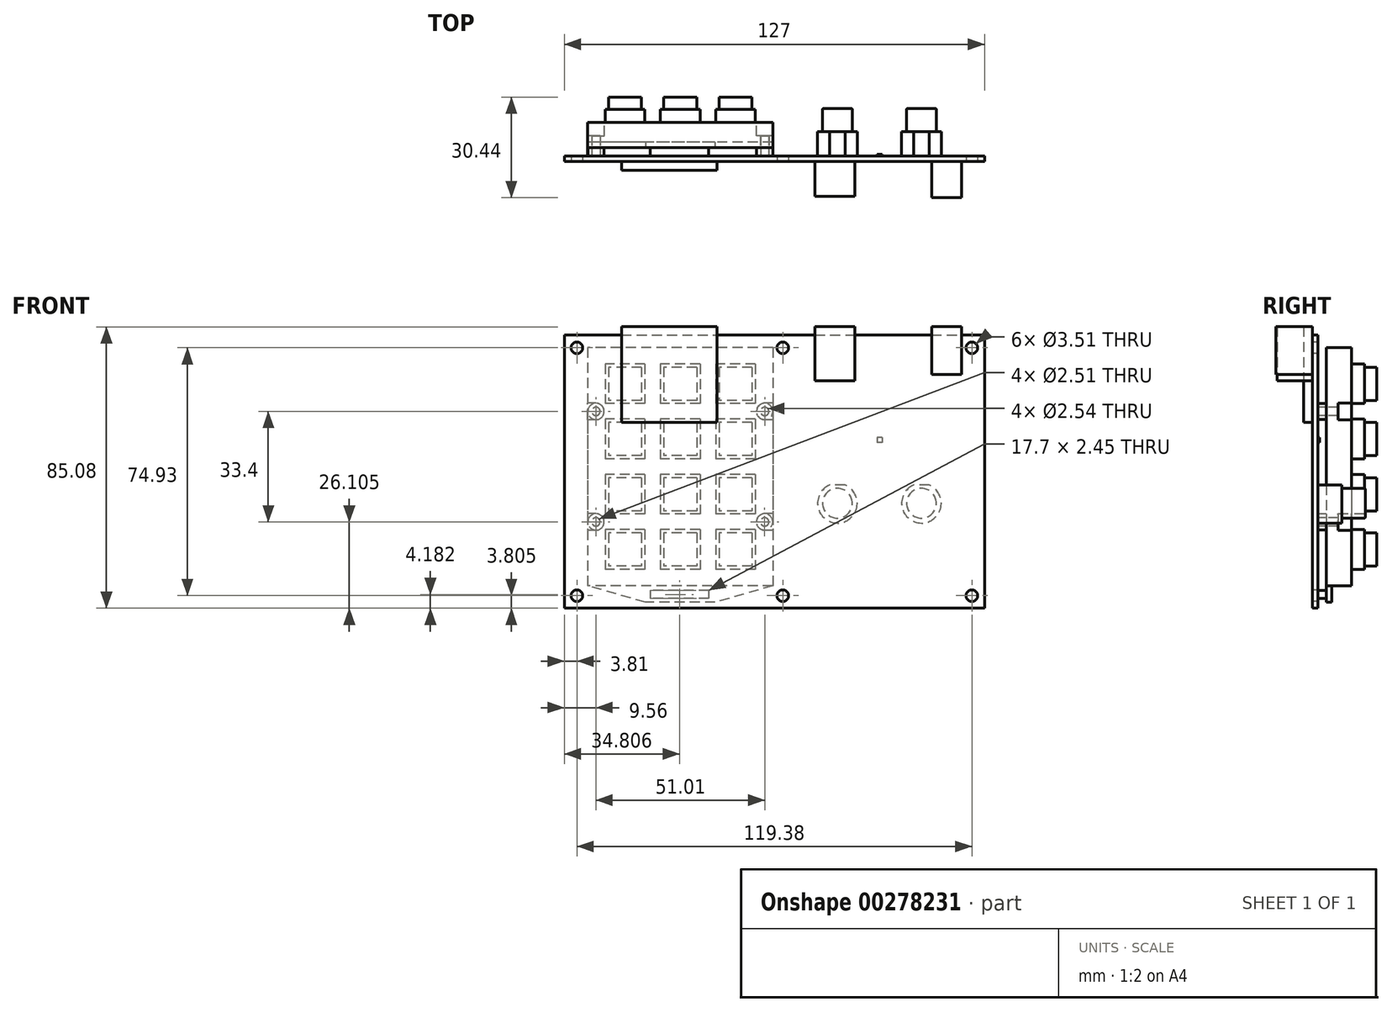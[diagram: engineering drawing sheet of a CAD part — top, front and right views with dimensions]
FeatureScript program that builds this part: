
annotation { "Feature Type Name" : "Feature", "Feature Type Description" : "" }
export const myFeature = defineFeature(function(context is Context, id is Id, definition is map)
    precondition{}
    {
        {
            var Q0;
            Q0=qCreatedBy(makeId("Front.planeOp"),FACE);
            var sketch = newSketch(context, id + "F0", { "sketchPlane" : qUnion([Q0])});
            skLineSegment(sketch, "E0.bottom", {"start": v(-63.5, 41.28) * mm, "end": v(63.5, 41.28) * mm});
            skLineSegment(sketch, "E0.top", {"start": v(-63.5, -41.28) * mm, "end": v(63.5, -41.28) * mm});
            skLineSegment(sketch, "E0.left", {"start": v(-63.5, 41.28) * mm, "end": v(-63.5, -41.28) * mm});
            skLineSegment(sketch, "E0.right", {"start": v(63.5, 41.28) * mm, "end": v(63.5, -41.28) * mm});
            skSolve(sketch);
        }
        {
            var Q0;
            Q0=makeQuery(id+"F0.imprint","IMPRINT",FACE,{"disambiguationData":[TD([[makeQuery(id+"F0.imprint","IMPRINT",EDGE,{"derivedFrom":sQuery(id+"F0.wireOp",EDGE,"E0.bottom")}),-1.0]])]});
            extrude(context, id + "F1", {"entities" : qUnion([Q0]), "depth" : 1.6 * mm});
        }
        {
            var Q0;
            Q0=makeQuery(id+"F1.opExtrude","CAP_FACE",FACE,{"disambiguationData":[OSD([sQuery(id+"F0.wireOp",EDGE,"E0.bottom"),sQuery(id+"F0.wireOp",EDGE,"E0.top"),sQuery(id+"F0.wireOp",EDGE,"E0.left"),sQuery(id+"F0.wireOp",EDGE,"E0.right")])],"isStart":false});
            var sketch = newSketch(context, id + "F2", { "sketchPlane" : qUnion([Q0])});
            skCircle(sketch, "E1", {"center": v(-59.7, 37.46) * mm, "radius": 1.75 * mm});
            skCircle(sketch, "E2", {"center": v(2.54, 37.46) * mm, "radius": 1.75 * mm});
            skCircle(sketch, "E3", {"center": v(59.7, 37.46) * mm, "radius": 1.75 * mm});
            skCircle(sketch, "E4", {"center": v(59.7, -37.47) * mm, "radius": 1.75 * mm});
            skCircle(sketch, "E5", {"center": v(2.54, -37.47) * mm, "radius": 1.75 * mm});
            skCircle(sketch, "E6", {"center": v(-59.7, -37.47) * mm, "radius": 1.75 * mm});
            skSolve(sketch);
        }
        {
            var Q0;
            Q0 = qSketchRegion(id + "F2", true);
            extrude(context, id + "F3", {"entities" : qUnion([Q0]), "operationType" : NewBodyOperationType.REMOVE, "oppositeDirection" : true, "depth" : 34.54 * mm});
        }
        {
            var Q0;
            Q0=makeQuery(id+"F1.opExtrude","CAP_FACE",FACE,{"disambiguationData":[OSD([sQuery(id+"F0.wireOp",EDGE,"E0.bottom"),sQuery(id+"F0.wireOp",EDGE,"E0.top"),sQuery(id+"F0.wireOp",EDGE,"E0.left"),sQuery(id+"F0.wireOp",EDGE,"E0.right")])],"isStart":false});
            var sketch = newSketch(context, id + "F4", { "sketchPlane" : qUnion([Q0])});
            skText(sketch, "E7", { "text": "Top\n", "fontName": "OpenSans-Regular.ttf"});
            const initialGuessF4  = {"E7": [-0.02127, 0.00143, 1, 0, 0.00758]};
            skSetInitialGuess(sketch, initialGuessF4);
            skSolve(sketch);
        }
        {
            var Q0;
            Q0=makeQuery(id+"F4.imprint","IMPRINT",FACE,{"disambiguationData":[TD([[makeQuery(id+"F4.imprint","IMPRINT",EDGE,{"derivedFrom":sQuery(id+"F4.wireOp",EDGE,"E7.sketch_text.stroke-0")}),1.0]])]});
            var sketch = newSketch(context, id + "F5", { "sketchPlane" : qUnion([Q0])});
            skLineSegment(sketch, "E8.bottom", {"start": v(-46.2, 43.82) * mm, "end": v(-17.3, 43.82) * mm});
            skLineSegment(sketch, "E8.top", {"start": v(-46.2, 14.92) * mm, "end": v(-17.3, 14.92) * mm});
            skLineSegment(sketch, "E8.left", {"start": v(-46.2, 43.82) * mm, "end": v(-46.2, 14.92) * mm});
            skLineSegment(sketch, "E8.right", {"start": v(-17.3, 43.82) * mm, "end": v(-17.3, 14.92) * mm});
            skLineSegment(sketch, "E9.bottom", {"start": v(12.27, 43.82) * mm, "end": v(24.3, 43.82) * mm});
            skLineSegment(sketch, "E9.top", {"start": v(12.27, 27.5) * mm, "end": v(24.3, 27.5) * mm});
            skLineSegment(sketch, "E9.left", {"start": v(12.27, 43.82) * mm, "end": v(12.27, 27.5) * mm});
            skLineSegment(sketch, "E9.right", {"start": v(24.3, 43.82) * mm, "end": v(24.3, 27.5) * mm});
            skLineSegment(sketch, "E10.bottom", {"start": v(47.52, 43.82) * mm, "end": v(56.51, 43.82) * mm});
            skLineSegment(sketch, "E10.top", {"start": v(47.52, 29.41) * mm, "end": v(56.51, 29.41) * mm});
            skLineSegment(sketch, "E10.left", {"start": v(47.52, 43.82) * mm, "end": v(47.52, 29.41) * mm});
            skLineSegment(sketch, "E10.right", {"start": v(56.51, 43.82) * mm, "end": v(56.51, 29.41) * mm});
            skSolve(sketch);
        }
        {
            var Q0;
            {var subQ0=sQuery(id+"F5.wireOp",EDGE,"E10.top");Q0=makeQuery(id+"F5.imprint","IMPRINT",FACE,{"disambiguationData":[TD([[makeQuery(id+"F5.imprint","IMPRINT",EDGE,{"derivedFrom":subQ0}),1.0]])]});}
            var Q1;
            {var subQ0=sQuery(id+"F5.wireOp",EDGE,"E10.bottom");Q1=makeQuery(id+"F5.imprint","IMPRINT",FACE,{"disambiguationData":[TD([[makeQuery(id+"F5.imprint","IMPRINT",EDGE,{"derivedFrom":subQ0}),-1.0]])]});}
            extrude(context, id + "F6", {"entities" : qUnion([Q0, Q1]), "operationType" : NewBodyOperationType.ADD, "depth" : 11 * mm});
        }
        {
            var Q0;
            {var subQ0=sQuery(id+"F5.wireOp",EDGE,"E9.top");Q0=makeQuery(id+"F5.imprint","IMPRINT",FACE,{"disambiguationData":[TD([[makeQuery(id+"F5.imprint","IMPRINT",EDGE,{"derivedFrom":subQ0}),1.0]])]});}
            var Q1;
            {var subQ0=sQuery(id+"F5.wireOp",EDGE,"E9.bottom");Q1=makeQuery(id+"F5.imprint","IMPRINT",FACE,{"disambiguationData":[TD([[makeQuery(id+"F5.imprint","IMPRINT",EDGE,{"derivedFrom":subQ0}),-1.0]])]});}
            extrude(context, id + "F7", {"entities" : qUnion([Q0, Q1]), "operationType" : NewBodyOperationType.ADD, "depth" : 10.62 * mm});
        }
        {
            var Q0;
            {var subQ0=sQuery(id+"F5.wireOp",EDGE,"E8.top");Q0=makeQuery(id+"F5.imprint","IMPRINT",FACE,{"disambiguationData":[TD([[makeQuery(id+"F5.imprint","IMPRINT",EDGE,{"derivedFrom":subQ0}),1.0]])]});}
            var Q1;
            {var subQ0=sQuery(id+"F5.wireOp",EDGE,"E8.bottom");Q1=makeQuery(id+"F5.imprint","IMPRINT",FACE,{"disambiguationData":[TD([[makeQuery(id+"F5.imprint","IMPRINT",EDGE,{"derivedFrom":subQ0}),-1.0]])]});}
            extrude(context, id + "F8", {"entities" : qUnion([Q0, Q1]), "operationType" : NewBodyOperationType.ADD, "depth" : 2.7 * mm});
        }
        {
            var Q0;
            Q0=makeQuery(id+"F1.opExtrude","CAP_FACE",FACE,{"disambiguationData":[OSD([sQuery(id+"F0.wireOp",EDGE,"E0.bottom"),sQuery(id+"F0.wireOp",EDGE,"E0.top"),sQuery(id+"F0.wireOp",EDGE,"E0.left"),sQuery(id+"F0.wireOp",EDGE,"E0.right")])],"isStart":true});
            var sketch = newSketch(context, id + "F9", { "sketchPlane" : qUnion([Q0])});
            skArc(sketch, "E11", {"start": v(-46.8, -4.01) * mm, "mid": v(-44.45, -15.52) * mm, "end": v(-42.1, -4.01) * mm});
            skArc(sketch, "E12", {"start": v(-21.4, -4.01) * mm, "mid": v(-19.05, -15.52) * mm, "end": v(-16.7, -4.01) * mm});
            skLineSegment(sketch, "E13", {"start": v(-46.8, -4.01) * mm, "end": v(-42.1, -4.01) * mm});
            skLineSegment(sketch, "E14.trimOffspring", {"start": v(-21.4, -4.01) * mm, "end": v(-16.7, -4.01) * mm});
            skSolve(sketch);
        }
        {
            var Q0;
            Q0 = qSketchRegion(id + "F9", true);
            extrude(context, id + "F10", {"entities" : qUnion([Q0]), "operationType" : NewBodyOperationType.ADD, "depth" : 7.34 * mm});
        }
        {
            var Q0;
            Q0=makeQuery(id+"F10.opExtrude","CAP_FACE",FACE,{"disambiguationData":[OSD([sQuery(id+"F9.wireOp",EDGE,"E11"),sQuery(id+"F9.wireOp",EDGE,"E13")])],"isStart":false});
            var sketch = newSketch(context, id + "F11", { "sketchPlane" : qUnion([Q0])});
            skCircle(sketch, "E15", {"center": v(-44.45, -9.53) * mm, "radius": 4.5 * mm});
            skCircle(sketch, "E16", {"center": v(-19.05, -9.53) * mm, "radius": 4.5 * mm});
            skSolve(sketch);
        }
        {
            var Q0;
            Q0 = qSketchRegion(id + "F11", true);
            extrude(context, id + "F12", {"entities" : qUnion([Q0]), "operationType" : NewBodyOperationType.ADD, "depth" : 7 * mm});
        }
        {
            var Q0;
            Q0=makeQuery(id+"F12.opExtrude","CAP_EDGE",EDGE,{"disambiguationData":[OSD([sQuery(id+"F11.wireOp",EDGE,"E15")])],"isStart":false});
            var Q1;
            Q1=makeQuery(id+"F12.opExtrude","CAP_EDGE",EDGE,{"disambiguationData":[OSD([sQuery(id+"F11.wireOp",EDGE,"E16")])],"isStart":false});
            fillet(context, id + "F13", {"entities" : qUnion([Q0, Q1]), "radius" : 0.25 * mm, "tangentPropagation" : true, "allowEdgeOverflow" : false});
        }
        {
            var Q0;
            Q0=makeQuery(id+"F1.opExtrude","CAP_FACE",FACE,{"disambiguationData":[OSD([sQuery(id+"F0.wireOp",EDGE,"E0.bottom"),sQuery(id+"F0.wireOp",EDGE,"E0.top"),sQuery(id+"F0.wireOp",EDGE,"E0.left"),sQuery(id+"F0.wireOp",EDGE,"E0.right")])],"isStart":true});
            var sketch = newSketch(context, id + "F14", { "sketchPlane" : qUnion([Q0])});
            skLineSegment(sketch, "E17.bottom", {"start": v(-32.51, 10.31) * mm, "end": v(-30.99, 10.31) * mm});
            skLineSegment(sketch, "E17.top", {"start": v(-32.51, 8.76) * mm, "end": v(-30.99, 8.76) * mm});
            skLineSegment(sketch, "E17.left", {"start": v(-32.51, 10.31) * mm, "end": v(-32.51, 8.76) * mm});
            skLineSegment(sketch, "E17.right", {"start": v(-30.99, 10.31) * mm, "end": v(-30.99, 8.76) * mm});
            skSolve(sketch);
        }
        {
            var Q0;
            Q0 = qSketchRegion(id + "F14", true);
            extrude(context, id + "F15", {"entities" : qUnion([Q0]), "operationType" : NewBodyOperationType.ADD, "depth" : 0.53 * mm});
        }
        {
            var Q0;
            Q0=makeQuery(id+"F1.opExtrude","CAP_FACE",FACE,{"disambiguationData":[OSD([sQuery(id+"F0.wireOp",EDGE,"E0.bottom"),sQuery(id+"F0.wireOp",EDGE,"E0.top"),sQuery(id+"F0.wireOp",EDGE,"E0.left"),sQuery(id+"F0.wireOp",EDGE,"E0.right")])],"isStart":true});
            var sketch = newSketch(context, id + "F16", { "sketchPlane" : qUnion([Q0])});
            skLineSegment(sketch, "E18.bottom", {"start": v(0.45, 37.53) * mm, "end": v(56.43, 37.53) * mm});
            skLineSegment(sketch, "E18.top", {"start": v(0.45, -34.47) * mm, "end": v(56.43, -34.47) * mm});
            skLineSegment(sketch, "E18.left", {"start": v(0.45, 37.53) * mm, "end": v(0.45, -34.47) * mm});
            skLineSegment(sketch, "E18.right", {"start": v(56.43, 37.53) * mm, "end": v(56.43, -34.47) * mm});
            skCircle(sketch, "E19", {"center": v(2.93, 18.23) * mm, "radius": 1.27 * mm});
            skCircle(sketch, "E20", {"center": v(2.94, -15.16) * mm, "radius": 1.27 * mm});
            skCircle(sketch, "E21", {"center": v(53.93, 18.23) * mm, "radius": 1.27 * mm});
            skCircle(sketch, "E22", {"center": v(53.94, -15.16) * mm, "radius": 1.27 * mm});
            skLineSegment(sketch, "E23", {"start": v(0.45, -34.47) * mm, "end": v(17.95, -39.46) * mm});
            skLineSegment(sketch, "E24", {"start": v(17.95, -39.46) * mm, "end": v(38.95, -39.46) * mm});
            skLineSegment(sketch, "E25", {"start": v(38.95, -39.46) * mm, "end": v(56.43, -34.47) * mm});
            skPoint(sketch, "E26", {"position": v(28.45, -37.47) * mm});
            skSolve(sketch);
        }
        {
            var Q0;
            Q0=makeQuery(id+"F16.imprint","IMPRINT",FACE,{"disambiguationData":[TD([[makeQuery(id+"F16.imprint","IMPRINT",EDGE,{"derivedFrom":sQuery(id+"F16.wireOp",EDGE,"E18.bottom")}),-1.0]])]});
            extrude(context, id + "F17", {"entities" : qUnion([Q0]), "depth" : 10.14 * mm, "hasSecondDirection" : true, "secondDirectionOppositeDirection" : false, "secondDirectionDepth" : 2.54 * mm});
        }
        {
            var Q0;
            Q0=makeQuery(id+"F16.imprint","IMPRINT",FACE,{"disambiguationData":[TD([[makeQuery(id+"F16.imprint","IMPRINT",EDGE,{"derivedFrom":sQuery(id+"F16.wireOp",EDGE,"E18.top")}),-1.0]])]});
            extrude(context, id + "F18", {"entities" : qUnion([Q0]), "operationType" : NewBodyOperationType.ADD, "depth" : 4.2 * mm, "hasSecondDirection" : true, "secondDirectionOppositeDirection" : false, "secondDirectionDepth" : 2.54 * mm});
        }
        {
            var Q0;
            Q0=makeQuery(id+"F17.opExtrude","CAP_FACE",FACE,{"disambiguationData":[OSD([sQuery(id+"F16.wireOp",EDGE,"E18.bottom"),sQuery(id+"F16.wireOp",EDGE,"E18.top"),sQuery(id+"F16.wireOp",EDGE,"E18.left"),sQuery(id+"F16.wireOp",EDGE,"E18.right"),sQuery(id+"F16.wireOp",EDGE,"E19"),sQuery(id+"F16.wireOp",EDGE,"E20"),sQuery(id+"F16.wireOp",EDGE,"E21"),sQuery(id+"F16.wireOp",EDGE,"E22")])],"isStart":false});
            var sketch = newSketch(context, id + "F19", { "sketchPlane" : qUnion([Q0])});
            skArc(sketch, "E27", {"start": v(53.93, 20.74) * mm, "mid": v(51.43, 18.23) * mm, "end": v(53.93, 15.73) * mm});
            skArc(sketch, "E28", {"start": v(53.94, -12.66) * mm, "mid": v(51.44, -15.16) * mm, "end": v(53.94, -17.67) * mm});
            skArc(sketch, "E29", {"start": v(0.45, -14.95) * mm, "mid": v(0.44, -15.16) * mm, "end": v(0.45, -15.38) * mm});
            skArc(sketch, "E30", {"start": v(0.45, 18.55) * mm, "mid": v(0.43, 18.23) * mm, "end": v(0.45, 17.92) * mm});
            skLineSegment(sketch, "E31", {"start": v(0.45, 20.74) * mm, "end": v(2.93, 20.74) * mm});
            skLineSegment(sketch, "E32", {"start": v(0.45, 15.73) * mm, "end": v(2.93, 15.73) * mm});
            skLineSegment(sketch, "E33", {"start": v(0.45, -12.66) * mm, "end": v(2.94, -12.66) * mm});
            skLineSegment(sketch, "E34", {"start": v(0.45, -17.67) * mm, "end": v(2.94, -17.67) * mm});
            skLineSegment(sketch, "E35", {"start": v(0.45, 20.74) * mm, "end": v(0.45, 15.73) * mm});
            skLineSegment(sketch, "E36", {"start": v(56.43, 20.74) * mm, "end": v(56.43, 15.73) * mm});
            skLineSegment(sketch, "E37", {"start": v(0.45, -12.66) * mm, "end": v(0.45, -17.67) * mm});
            skLineSegment(sketch, "E38", {"start": v(56.43, -12.66) * mm, "end": v(56.43, -17.67) * mm});
            skArc(sketch, "E39.trimOffspring", {"start": v(2.93, 15.73) * mm, "mid": v(5.43, 18.23) * mm, "end": v(2.93, 20.74) * mm});
            skArc(sketch, "E40.trimOffspring", {"start": v(56.43, 18.12) * mm, "mid": v(56.43, 18.23) * mm, "end": v(56.43, 18.35) * mm});
            skArc(sketch, "E41.trimOffspring", {"start": v(56.43, -15.42) * mm, "mid": v(56.44, -15.16) * mm, "end": v(56.43, -14.91) * mm});
            skLineSegment(sketch, "E42.trimOffspring", {"start": v(53.93, 15.73) * mm, "end": v(56.43, 15.73) * mm});
            skLineSegment(sketch, "E43.trimOffspring", {"start": v(53.93, 20.74) * mm, "end": v(56.43, 20.74) * mm});
            skArc(sketch, "E44.trimOffspring", {"start": v(2.94, -17.67) * mm, "mid": v(5.44, -15.16) * mm, "end": v(2.94, -12.66) * mm});
            skLineSegment(sketch, "E45.trimOffspring", {"start": v(53.94, -17.67) * mm, "end": v(56.43, -17.67) * mm});
            skLineSegment(sketch, "E46.trimOffspring", {"start": v(53.94, -12.66) * mm, "end": v(56.43, -12.66) * mm});
            skSolve(sketch);
        }
        {
            var Q0;
            Q0 = qSketchRegion(id + "F19", true);
            extrude(context, id + "F20", {"entities" : qUnion([Q0]), "operationType" : NewBodyOperationType.REMOVE, "oppositeDirection" : true, "depth" : 4 * mm});
        }
        {
            var Q0;
            Q0=makeQuery(id+"F17.opExtrude","CAP_FACE",FACE,{"disambiguationData":[OSD([sQuery(id+"F16.wireOp",EDGE,"E18.bottom"),sQuery(id+"F16.wireOp",EDGE,"E18.top"),sQuery(id+"F16.wireOp",EDGE,"E18.left"),sQuery(id+"F16.wireOp",EDGE,"E18.right"),sQuery(id+"F16.wireOp",EDGE,"E19"),sQuery(id+"F16.wireOp",EDGE,"E20"),sQuery(id+"F16.wireOp",EDGE,"E21"),sQuery(id+"F16.wireOp",EDGE,"E22")])],"isStart":false});
            var sketch = newSketch(context, id + "F21", { "sketchPlane" : qUnion([Q0])});
            skLineSegment(sketch, "E47.bottom", {"start": v(5.75, -17.52) * mm, "end": v(17.75, -17.52) * mm});
            skLineSegment(sketch, "E47.top", {"start": v(5.75, -29.52) * mm, "end": v(17.75, -29.52) * mm});
            skLineSegment(sketch, "E47.left", {"start": v(5.75, -17.52) * mm, "end": v(5.75, -29.52) * mm});
            skLineSegment(sketch, "E47.right", {"start": v(17.75, -17.52) * mm, "end": v(17.75, -29.52) * mm});
            skLineSegment(sketch, "E48.0.1.0", {"start": v(5.75, -0.82) * mm, "end": v(17.75, -0.82) * mm});
            skLineSegment(sketch, "E48.0.1.1", {"start": v(17.75, -0.82) * mm, "end": v(17.75, -12.82) * mm});
            skLineSegment(sketch, "E48.0.1.2", {"start": v(5.75, -12.82) * mm, "end": v(17.75, -12.82) * mm});
            skLineSegment(sketch, "E48.0.1.3", {"start": v(5.75, -0.82) * mm, "end": v(5.75, -12.82) * mm});
            skLineSegment(sketch, "E48.0.2.0", {"start": v(5.75, 15.88) * mm, "end": v(17.75, 15.88) * mm});
            skLineSegment(sketch, "E48.0.2.1", {"start": v(17.75, 15.88) * mm, "end": v(17.75, 3.88) * mm});
            skLineSegment(sketch, "E48.0.2.2", {"start": v(5.75, 3.88) * mm, "end": v(17.75, 3.88) * mm});
            skLineSegment(sketch, "E48.0.2.3", {"start": v(5.75, 15.88) * mm, "end": v(5.75, 3.88) * mm});
            skLineSegment(sketch, "E48.0.3.0", {"start": v(5.75, 32.58) * mm, "end": v(17.75, 32.58) * mm});
            skLineSegment(sketch, "E48.0.3.1", {"start": v(17.75, 32.58) * mm, "end": v(17.75, 20.58) * mm});
            skLineSegment(sketch, "E48.0.3.2", {"start": v(5.75, 20.58) * mm, "end": v(17.75, 20.58) * mm});
            skLineSegment(sketch, "E48.0.3.3", {"start": v(5.75, 32.58) * mm, "end": v(5.75, 20.58) * mm});
            skLineSegment(sketch, "E48.1.0.0", {"start": v(22.45, -17.52) * mm, "end": v(34.45, -17.52) * mm});
            skLineSegment(sketch, "E48.1.0.1", {"start": v(34.45, -17.52) * mm, "end": v(34.45, -29.52) * mm});
            skLineSegment(sketch, "E48.1.0.2", {"start": v(22.45, -29.52) * mm, "end": v(34.45, -29.52) * mm});
            skLineSegment(sketch, "E48.1.0.3", {"start": v(22.45, -17.52) * mm, "end": v(22.45, -29.52) * mm});
            skLineSegment(sketch, "E48.1.1.0", {"start": v(22.45, -0.82) * mm, "end": v(34.45, -0.82) * mm});
            skLineSegment(sketch, "E48.1.1.1", {"start": v(34.45, -0.82) * mm, "end": v(34.45, -12.82) * mm});
            skLineSegment(sketch, "E48.1.1.2", {"start": v(22.45, -12.82) * mm, "end": v(34.45, -12.82) * mm});
            skLineSegment(sketch, "E48.1.1.3", {"start": v(22.45, -0.82) * mm, "end": v(22.45, -12.82) * mm});
            skLineSegment(sketch, "E48.1.2.0", {"start": v(22.45, 15.88) * mm, "end": v(34.45, 15.88) * mm});
            skLineSegment(sketch, "E48.1.2.1", {"start": v(34.45, 15.88) * mm, "end": v(34.45, 3.88) * mm});
            skLineSegment(sketch, "E48.1.2.2", {"start": v(22.45, 3.88) * mm, "end": v(34.45, 3.88) * mm});
            skLineSegment(sketch, "E48.1.2.3", {"start": v(22.45, 15.88) * mm, "end": v(22.45, 3.88) * mm});
            skLineSegment(sketch, "E48.1.3.0", {"start": v(22.45, 32.58) * mm, "end": v(34.45, 32.58) * mm});
            skLineSegment(sketch, "E48.1.3.1", {"start": v(34.45, 32.58) * mm, "end": v(34.45, 20.58) * mm});
            skLineSegment(sketch, "E48.1.3.2", {"start": v(22.45, 20.58) * mm, "end": v(34.45, 20.58) * mm});
            skLineSegment(sketch, "E48.1.3.3", {"start": v(22.45, 32.58) * mm, "end": v(22.45, 20.58) * mm});
            skLineSegment(sketch, "E48.2.0.0", {"start": v(39.15, -17.52) * mm, "end": v(51.15, -17.52) * mm});
            skLineSegment(sketch, "E48.2.0.1", {"start": v(51.15, -17.52) * mm, "end": v(51.15, -29.52) * mm});
            skLineSegment(sketch, "E48.2.0.2", {"start": v(39.15, -29.52) * mm, "end": v(51.15, -29.52) * mm});
            skLineSegment(sketch, "E48.2.0.3", {"start": v(39.15, -17.52) * mm, "end": v(39.15, -29.52) * mm});
            skLineSegment(sketch, "E48.2.1.0", {"start": v(39.15, -0.82) * mm, "end": v(51.15, -0.82) * mm});
            skLineSegment(sketch, "E48.2.1.1", {"start": v(51.15, -0.82) * mm, "end": v(51.15, -12.82) * mm});
            skLineSegment(sketch, "E48.2.1.2", {"start": v(39.15, -12.82) * mm, "end": v(51.15, -12.82) * mm});
            skLineSegment(sketch, "E48.2.1.3", {"start": v(39.15, -0.82) * mm, "end": v(39.15, -12.82) * mm});
            skLineSegment(sketch, "E48.2.2.0", {"start": v(39.15, 15.88) * mm, "end": v(51.15, 15.88) * mm});
            skLineSegment(sketch, "E48.2.2.1", {"start": v(51.15, 15.88) * mm, "end": v(51.15, 3.88) * mm});
            skLineSegment(sketch, "E48.2.2.2", {"start": v(39.15, 3.88) * mm, "end": v(51.15, 3.88) * mm});
            skLineSegment(sketch, "E48.2.2.3", {"start": v(39.15, 15.88) * mm, "end": v(39.15, 3.88) * mm});
            skLineSegment(sketch, "E48.2.3.0", {"start": v(39.15, 32.58) * mm, "end": v(51.15, 32.58) * mm});
            skLineSegment(sketch, "E48.2.3.1", {"start": v(51.15, 32.58) * mm, "end": v(51.15, 20.58) * mm});
            skLineSegment(sketch, "E48.2.3.2", {"start": v(39.15, 20.58) * mm, "end": v(51.15, 20.58) * mm});
            skLineSegment(sketch, "E48.2.3.3", {"start": v(39.15, 32.58) * mm, "end": v(39.15, 20.58) * mm});
            skLineSegment(sketch, "E48.direction1", {"start": v(5.75, -29.52) * mm, "end": v(22.45, -29.52) * mm, "construction": true});
            skLineSegment(sketch, "E48.direction2", {"start": v(5.75, -29.52) * mm, "end": v(5.75, -12.82) * mm, "construction": true});
            skLineSegment(sketch, "E49.bottom", {"start": v(6.75, -18.52) * mm, "end": v(16.75, -18.52) * mm});
            skLineSegment(sketch, "E49.top", {"start": v(6.75, -28.52) * mm, "end": v(16.75, -28.52) * mm});
            skLineSegment(sketch, "E49.left", {"start": v(6.75, -18.52) * mm, "end": v(6.75, -28.52) * mm});
            skLineSegment(sketch, "E49.right", {"start": v(16.75, -18.52) * mm, "end": v(16.75, -28.52) * mm});
            skLineSegment(sketch, "E50.0.1.0", {"start": v(6.75, -1.82) * mm, "end": v(16.75, -1.82) * mm});
            skLineSegment(sketch, "E50.0.1.1", {"start": v(6.75, -1.82) * mm, "end": v(6.75, -11.82) * mm});
            skLineSegment(sketch, "E50.0.1.2", {"start": v(6.75, -11.82) * mm, "end": v(16.75, -11.82) * mm});
            skLineSegment(sketch, "E50.0.1.3", {"start": v(16.75, -1.82) * mm, "end": v(16.75, -11.82) * mm});
            skLineSegment(sketch, "E50.0.2.0", {"start": v(6.75, 14.88) * mm, "end": v(16.75, 14.88) * mm});
            skLineSegment(sketch, "E50.0.2.1", {"start": v(6.75, 14.88) * mm, "end": v(6.75, 4.88) * mm});
            skLineSegment(sketch, "E50.0.2.2", {"start": v(6.75, 4.88) * mm, "end": v(16.75, 4.88) * mm});
            skLineSegment(sketch, "E50.0.2.3", {"start": v(16.75, 14.88) * mm, "end": v(16.75, 4.88) * mm});
            skLineSegment(sketch, "E50.0.3.0", {"start": v(6.75, 31.58) * mm, "end": v(16.75, 31.58) * mm});
            skLineSegment(sketch, "E50.0.3.1", {"start": v(6.75, 31.58) * mm, "end": v(6.75, 21.58) * mm});
            skLineSegment(sketch, "E50.0.3.2", {"start": v(6.75, 21.58) * mm, "end": v(16.75, 21.58) * mm});
            skLineSegment(sketch, "E50.0.3.3", {"start": v(16.75, 31.58) * mm, "end": v(16.75, 21.58) * mm});
            skLineSegment(sketch, "E50.1.0.0", {"start": v(23.45, -18.52) * mm, "end": v(33.45, -18.52) * mm});
            skLineSegment(sketch, "E50.1.0.1", {"start": v(23.45, -18.52) * mm, "end": v(23.45, -28.52) * mm});
            skLineSegment(sketch, "E50.1.0.2", {"start": v(23.45, -28.52) * mm, "end": v(33.45, -28.52) * mm});
            skLineSegment(sketch, "E50.1.0.3", {"start": v(33.45, -18.52) * mm, "end": v(33.45, -28.52) * mm});
            skLineSegment(sketch, "E50.1.1.0", {"start": v(23.45, -1.82) * mm, "end": v(33.45, -1.82) * mm});
            skLineSegment(sketch, "E50.1.1.1", {"start": v(23.45, -1.82) * mm, "end": v(23.45, -11.82) * mm});
            skLineSegment(sketch, "E50.1.1.2", {"start": v(23.45, -11.82) * mm, "end": v(33.45, -11.82) * mm});
            skLineSegment(sketch, "E50.1.1.3", {"start": v(33.45, -1.82) * mm, "end": v(33.45, -11.82) * mm});
            skLineSegment(sketch, "E50.1.2.0", {"start": v(23.45, 14.88) * mm, "end": v(33.45, 14.88) * mm});
            skLineSegment(sketch, "E50.1.2.1", {"start": v(23.45, 14.88) * mm, "end": v(23.45, 4.88) * mm});
            skLineSegment(sketch, "E50.1.2.2", {"start": v(23.45, 4.88) * mm, "end": v(33.45, 4.88) * mm});
            skLineSegment(sketch, "E50.1.2.3", {"start": v(33.45, 14.88) * mm, "end": v(33.45, 4.88) * mm});
            skLineSegment(sketch, "E50.1.3.0", {"start": v(23.45, 31.58) * mm, "end": v(33.45, 31.58) * mm});
            skLineSegment(sketch, "E50.1.3.1", {"start": v(23.45, 31.58) * mm, "end": v(23.45, 21.58) * mm});
            skLineSegment(sketch, "E50.1.3.2", {"start": v(23.45, 21.58) * mm, "end": v(33.45, 21.58) * mm});
            skLineSegment(sketch, "E50.1.3.3", {"start": v(33.45, 31.58) * mm, "end": v(33.45, 21.58) * mm});
            skLineSegment(sketch, "E50.2.0.0", {"start": v(40.15, -18.52) * mm, "end": v(50.15, -18.52) * mm});
            skLineSegment(sketch, "E50.2.0.1", {"start": v(40.15, -18.52) * mm, "end": v(40.15, -28.52) * mm});
            skLineSegment(sketch, "E50.2.0.2", {"start": v(40.15, -28.52) * mm, "end": v(50.15, -28.52) * mm});
            skLineSegment(sketch, "E50.2.0.3", {"start": v(50.15, -18.52) * mm, "end": v(50.15, -28.52) * mm});
            skLineSegment(sketch, "E50.2.1.0", {"start": v(40.15, -1.82) * mm, "end": v(50.15, -1.82) * mm});
            skLineSegment(sketch, "E50.2.1.1", {"start": v(40.15, -1.82) * mm, "end": v(40.15, -11.82) * mm});
            skLineSegment(sketch, "E50.2.1.2", {"start": v(40.15, -11.82) * mm, "end": v(50.15, -11.82) * mm});
            skLineSegment(sketch, "E50.2.1.3", {"start": v(50.15, -1.82) * mm, "end": v(50.15, -11.82) * mm});
            skLineSegment(sketch, "E50.2.2.0", {"start": v(40.15, 14.88) * mm, "end": v(50.15, 14.88) * mm});
            skLineSegment(sketch, "E50.2.2.1", {"start": v(40.15, 14.88) * mm, "end": v(40.15, 4.88) * mm});
            skLineSegment(sketch, "E50.2.2.2", {"start": v(40.15, 4.88) * mm, "end": v(50.15, 4.88) * mm});
            skLineSegment(sketch, "E50.2.2.3", {"start": v(50.15, 14.88) * mm, "end": v(50.15, 4.88) * mm});
            skLineSegment(sketch, "E50.2.3.0", {"start": v(40.15, 31.58) * mm, "end": v(50.15, 31.58) * mm});
            skLineSegment(sketch, "E50.2.3.1", {"start": v(40.15, 31.58) * mm, "end": v(40.15, 21.58) * mm});
            skLineSegment(sketch, "E50.2.3.2", {"start": v(40.15, 21.58) * mm, "end": v(50.15, 21.58) * mm});
            skLineSegment(sketch, "E50.2.3.3", {"start": v(50.15, 31.58) * mm, "end": v(50.15, 21.58) * mm});
            skLineSegment(sketch, "E50.direction1", {"start": v(6.75, -28.52) * mm, "end": v(23.45, -28.52) * mm, "construction": true});
            skLineSegment(sketch, "E50.direction2", {"start": v(6.75, -28.52) * mm, "end": v(6.75, -11.82) * mm, "construction": true});
            skSolve(sketch);
        }
        {
            var Q0;
            Q0 = qSketchRegion(id + "F21", true);
            extrude(context, id + "F22", {"entities" : qUnion([Q0]), "operationType" : NewBodyOperationType.ADD, "depth" : 4 * mm});
        }
        {
            var Q0;
            Q0=makeQuery(id+"F21.imprint","IMPRINT",FACE,{"disambiguationData":[TD([[makeQuery(id+"F21.imprint","IMPRINT",EDGE,{"derivedFrom":sQuery(id+"F21.wireOp",EDGE,"E49.bottom")}),-1.0]])]});
            var Q1;
            Q1=makeQuery(id+"F21.imprint","IMPRINT",FACE,{"disambiguationData":[TD([[makeQuery(id+"F21.imprint","IMPRINT",EDGE,{"derivedFrom":sQuery(id+"F21.wireOp",EDGE,"E50.1.0.0")}),-1.0]])]});
            var Q2;
            Q2=makeQuery(id+"F21.imprint","IMPRINT",FACE,{"disambiguationData":[TD([[makeQuery(id+"F21.imprint","IMPRINT",EDGE,{"derivedFrom":sQuery(id+"F21.wireOp",EDGE,"E50.2.0.0")}),-1.0]])]});
            var Q3;
            Q3=makeQuery(id+"F21.imprint","IMPRINT",FACE,{"disambiguationData":[TD([[makeQuery(id+"F21.imprint","IMPRINT",EDGE,{"derivedFrom":sQuery(id+"F21.wireOp",EDGE,"E50.2.1.0")}),-1.0]])]});
            var Q4;
            Q4=makeQuery(id+"F21.imprint","IMPRINT",FACE,{"disambiguationData":[TD([[makeQuery(id+"F21.imprint","IMPRINT",EDGE,{"derivedFrom":sQuery(id+"F21.wireOp",EDGE,"E50.0.1.0")}),-1.0]])]});
            var Q5;
            Q5=makeQuery(id+"F21.imprint","IMPRINT",FACE,{"disambiguationData":[TD([[makeQuery(id+"F21.imprint","IMPRINT",EDGE,{"derivedFrom":sQuery(id+"F21.wireOp",EDGE,"E50.1.1.0")}),-1.0]])]});
            var Q6;
            Q6=makeQuery(id+"F21.imprint","IMPRINT",FACE,{"disambiguationData":[TD([[makeQuery(id+"F21.imprint","IMPRINT",EDGE,{"derivedFrom":sQuery(id+"F21.wireOp",EDGE,"E50.0.2.0")}),-1.0]])]});
            var Q7;
            Q7=makeQuery(id+"F21.imprint","IMPRINT",FACE,{"disambiguationData":[TD([[makeQuery(id+"F21.imprint","IMPRINT",EDGE,{"derivedFrom":sQuery(id+"F21.wireOp",EDGE,"E50.1.2.0")}),-1.0]])]});
            var Q8;
            Q8=makeQuery(id+"F21.imprint","IMPRINT",FACE,{"disambiguationData":[TD([[makeQuery(id+"F21.imprint","IMPRINT",EDGE,{"derivedFrom":sQuery(id+"F21.wireOp",EDGE,"E50.2.2.0")}),-1.0]])]});
            var Q9;
            Q9=makeQuery(id+"F21.imprint","IMPRINT",FACE,{"disambiguationData":[TD([[makeQuery(id+"F21.imprint","IMPRINT",EDGE,{"derivedFrom":sQuery(id+"F21.wireOp",EDGE,"E50.2.3.0")}),-1.0]])]});
            var Q10;
            Q10=makeQuery(id+"F21.imprint","IMPRINT",FACE,{"disambiguationData":[TD([[makeQuery(id+"F21.imprint","IMPRINT",EDGE,{"derivedFrom":sQuery(id+"F21.wireOp",EDGE,"E50.1.3.0")}),-1.0]])]});
            var Q11;
            Q11=makeQuery(id+"F21.imprint","IMPRINT",FACE,{"disambiguationData":[TD([[makeQuery(id+"F21.imprint","IMPRINT",EDGE,{"derivedFrom":sQuery(id+"F21.wireOp",EDGE,"E50.0.3.0")}),-1.0]])]});
            extrude(context, id + "F23", {"entities" : qUnion([Q0, Q1, Q2, Q3, Q4, Q5, Q6, Q7, Q8, Q9, Q10, Q11]), "operationType" : NewBodyOperationType.ADD, "depth" : 7.7 * mm});
        }
        {
            var Q0;
            Q0=makeQuery(id+"F1.opExtrude","CAP_FACE",FACE,{"disambiguationData":[OSD([sQuery(id+"F0.wireOp",EDGE,"E0.bottom"),sQuery(id+"F0.wireOp",EDGE,"E0.top"),sQuery(id+"F0.wireOp",EDGE,"E0.left"),sQuery(id+"F0.wireOp",EDGE,"E0.right")])],"isStart":true});
            var sketch = newSketch(context, id + "F24", { "sketchPlane" : qUnion([Q0])});
            skLineSegment(sketch, "E51.bottom", {"start": v(19.84, -35.86) * mm, "end": v(37.54, -35.86) * mm});
            skLineSegment(sketch, "E51.top", {"start": v(19.84, -38.31) * mm, "end": v(37.54, -38.31) * mm});
            skLineSegment(sketch, "E51.left", {"start": v(19.84, -35.86) * mm, "end": v(19.84, -38.31) * mm});
            skLineSegment(sketch, "E51.right", {"start": v(37.54, -35.86) * mm, "end": v(37.54, -38.31) * mm});
            skSolve(sketch);
        }
        {
            var Q0;
            Q0 = qSketchRegion(id + "F24", true);
            extrude(context, id + "F25", {"entities" : qUnion([Q0]), "operationType" : NewBodyOperationType.ADD, "depth" : 2.8 * mm});
        }
        {
            var Q0;
            Q0=makeQuery(id+"F1.opExtrude","CAP_FACE",FACE,{"disambiguationData":[OSD([sQuery(id+"F0.wireOp",EDGE,"E0.bottom"),sQuery(id+"F0.wireOp",EDGE,"E0.top"),sQuery(id+"F0.wireOp",EDGE,"E0.left"),sQuery(id+"F0.wireOp",EDGE,"E0.right")])],"isStart":true});
            var sketch = newSketch(context, id + "F26", { "sketchPlane" : qUnion([Q0])});
            skCircle(sketch, "E52", {"center": v(2.93, 18.23) * mm, "radius": 2.46 * mm});
            skCircle(sketch, "E53", {"center": v(2.93, 18.23) * mm, "radius": 1.25 * mm});
            skCircle(sketch, "E54.0.1.0", {"center": v(2.94, -15.16) * mm, "radius": 1.25 * mm});
            skCircle(sketch, "E54.0.1.1", {"center": v(2.94, -15.16) * mm, "radius": 2.46 * mm});
            skCircle(sketch, "E54.1.0.0", {"center": v(53.93, 18.23) * mm, "radius": 1.25 * mm});
            skCircle(sketch, "E54.1.0.1", {"center": v(53.93, 18.23) * mm, "radius": 2.46 * mm});
            skCircle(sketch, "E54.1.1.0", {"center": v(53.94, -15.16) * mm, "radius": 1.25 * mm});
            skCircle(sketch, "E54.1.1.1", {"center": v(53.94, -15.16) * mm, "radius": 2.46 * mm});
            skSolve(sketch);
        }
        {
            var Q0;
            Q0 = qSketchRegion(id + "F26", true);
            extrude(context, id + "F27", {"entities" : qUnion([Q0]), "depth" : 2.54 * mm});
        }
    });
